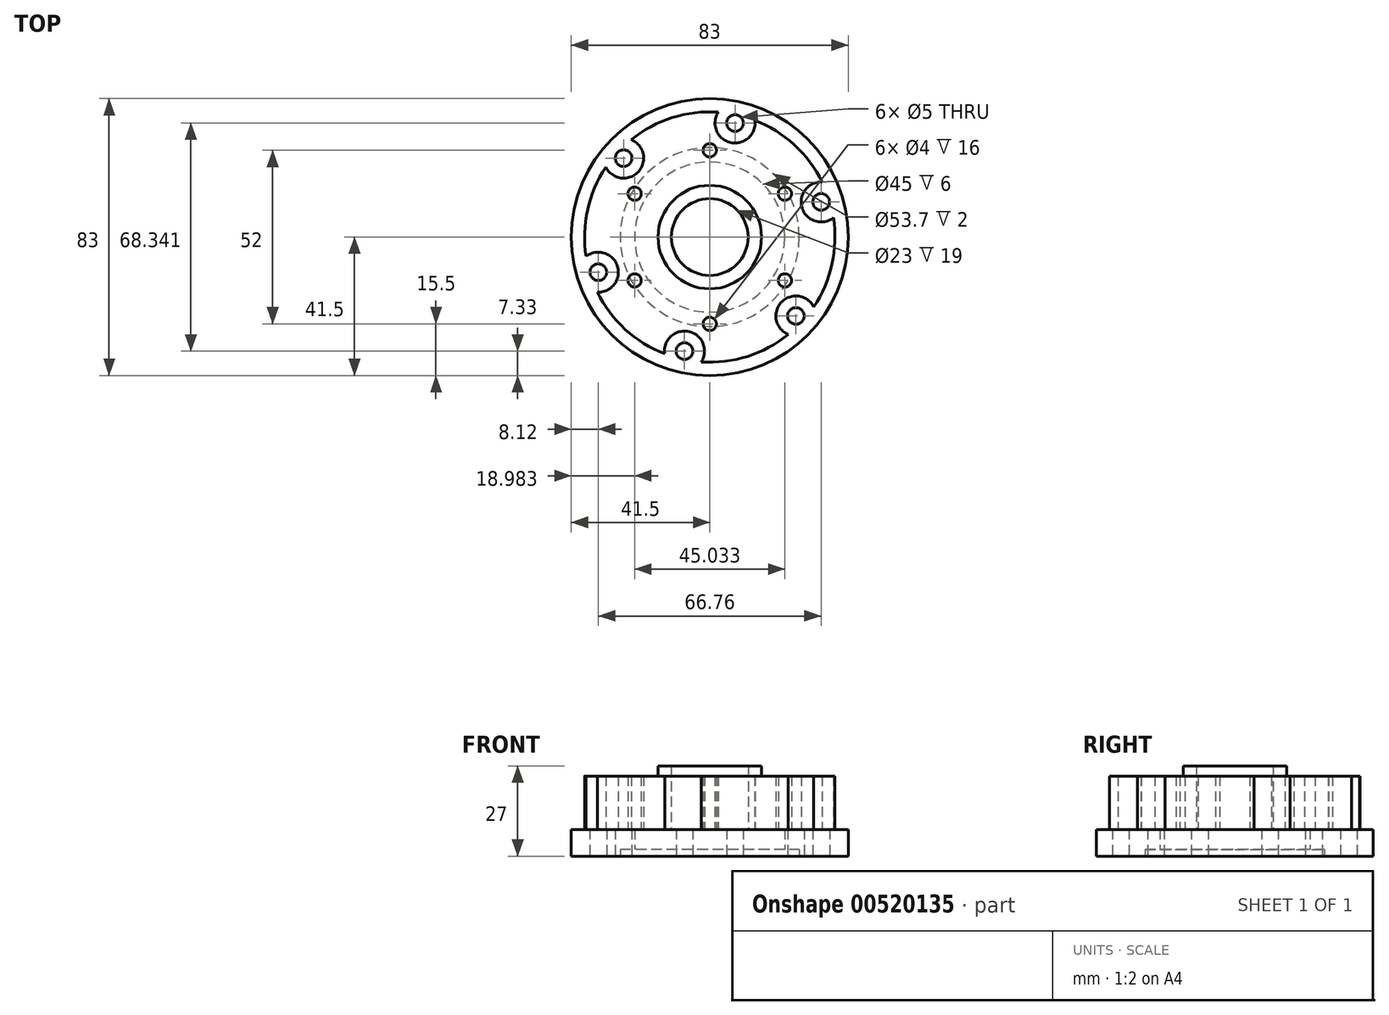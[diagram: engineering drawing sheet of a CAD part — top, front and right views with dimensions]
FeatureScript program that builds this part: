
annotation { "Feature Type Name" : "Feature", "Feature Type Description" : "" }
export const myFeature = defineFeature(function(context is Context, id is Id, definition is map)
    precondition{}
    {
        {
            var Q0;
            Q0=qCreatedBy(makeId("Top.planeOp"),FACE);
            var sketch = newSketch(context, id + "F0", { "sketchPlane" : qUnion([Q0])});
            skCircle(sketch, "E0", {"center": v(0, 0) * mm, "radius": 41.5 * mm});
            skLineSegment(sketch, "E1", {"start": v(0, 0) * mm, "end": v(-13.8, -62.28) * mm, "construction": true});
            skCircle(sketch, "E2", {"center": v(0, 0) * mm, "radius": 35 * mm, "construction": true});
            skCircle(sketch, "E3", {"center": v(-7.58, -34.17) * mm, "radius": 2.5 * mm});
            skCircle(sketch, "E4.1.0", {"center": v(25.8, -23.65) * mm, "radius": 2.5 * mm});
            skCircle(sketch, "E4.2.0", {"center": v(33.38, 10.52) * mm, "radius": 2.5 * mm});
            skCircle(sketch, "E5.1.3.0", {"center": v(7.58, 34.17) * mm, "radius": 2.5 * mm});
            skCircle(sketch, "E5.1.4.0", {"center": v(-25.8, 23.65) * mm, "radius": 2.5 * mm});
            skCircle(sketch, "E5.1.5.0", {"center": v(-33.38, -10.52) * mm, "radius": 2.5 * mm});
            skCircle(sketch, "E6", {"center": v(0, 0) * mm, "radius": 26.85 * mm});
            skCircle(sketch, "E7", {"center": v(0, 0) * mm, "radius": 22.5 * mm});
            skSolve(sketch);
        }
        {
            var Q0;
            Q0=makeQuery(id+"F0.imprint","IMPRINT",FACE,{"disambiguationData":[TD([[makeQuery(id+"F0.imprint","IMPRINT",EDGE,{"derivedFrom":sQuery(id+"F0.wireOp",EDGE,"E0")}),1.0]])]});
            var Q1;
            Q1=makeQuery(id+"F0.imprint","IMPRINT",FACE,{"disambiguationData":[TD([[makeQuery(id+"F0.imprint","IMPRINT",EDGE,{"derivedFrom":sQuery(id+"F0.wireOp",EDGE,"E6")}),1.0]])]});
            extrude(context, id + "F1", {"entities" : qUnion([Q0, Q1]), "depth" : 8 * mm, "offsetDistance" : 25 * mm});
        }
        {
            var Q0;
            Q0=makeQuery(id+"F0.imprint","IMPRINT",FACE,{"disambiguationData":[TD([[makeQuery(id+"F0.imprint","IMPRINT",EDGE,{"derivedFrom":sQuery(id+"F0.wireOp",EDGE,"E6")}),1.0]])]});
            extrude(context, id + "F2", {"entities" : qUnion([Q0]), "operationType" : NewBodyOperationType.REMOVE, "depth" : 2 * mm, "offsetDistance" : 25 * mm});
        }
        {
            var Q0;
            Q0=makeQuery(id+"F1.opExtrude","CAP_FACE",FACE,{"disambiguationData":[OSD([sQuery(id+"F0.wireOp",EDGE,"E0"),sQuery(id+"F0.wireOp",EDGE,"E3"),sQuery(id+"F0.wireOp",EDGE,"E4.1.0"),sQuery(id+"F0.wireOp",EDGE,"E4.2.0"),sQuery(id+"F0.wireOp",EDGE,"E5.1.3.0"),sQuery(id+"F0.wireOp",EDGE,"E5.1.4.0"),sQuery(id+"F0.wireOp",EDGE,"E5.1.5.0"),sQuery(id+"F0.wireOp",EDGE,"E7")])],"isStart":false});
            var sketch = newSketch(context, id + "F3", { "sketchPlane" : qUnion([Q0])});
            skCircle(sketch, "E8", {"center": v(0, 0) * mm, "radius": 37.5 * mm});
            skCircle(sketch, "E9", {"center": v(0, 0) * mm, "radius": 26 * mm, "construction": true});
            skCircle(sketch, "E10", {"center": v(0, 26) * mm, "radius": 2 * mm});
            skCircle(sketch, "E11.1.0", {"center": v(-22.52, 13) * mm, "radius": 2 * mm});
            skCircle(sketch, "E11.2.0", {"center": v(-22.52, -13) * mm, "radius": 2 * mm});
            skCircle(sketch, "E11.3.0", {"center": v(0, -26) * mm, "radius": 2 * mm});
            skCircle(sketch, "E11.4.0", {"center": v(22.52, -13) * mm, "radius": 2 * mm});
            skCircle(sketch, "E11.5.0", {"center": v(22.52, 13) * mm, "radius": 2 * mm});
            skCircle(sketch, "E12", {"center": v(0, 0) * mm, "radius": 11.5 * mm});
            skCircle(sketch, "E13", {"center": v(-25.8, 23.65) * mm, "radius": 6 * mm});
            skCircle(sketch, "E14.1.0", {"center": v(-33.38, -10.52) * mm, "radius": 6 * mm});
            skCircle(sketch, "E14.2.0", {"center": v(-7.58, -34.17) * mm, "radius": 6 * mm});
            skCircle(sketch, "E14.3.0", {"center": v(25.8, -23.65) * mm, "radius": 6 * mm});
            skCircle(sketch, "E14.4.0", {"center": v(33.38, 10.52) * mm, "radius": 6 * mm});
            skCircle(sketch, "E14.5.0", {"center": v(7.58, 34.17) * mm, "radius": 6 * mm});
            skSolve(sketch);
        }
        {
            var Q0;
            {var subQ6=sQuery(id+"F3.wireOp",EDGE,"E8");var subQ34=sQuery(id+"F3.wireOp",EDGE,"E14.4.0");var subQ35=makeQuery(id+"F3.imprint","INTERSECT",VERTEX,{"disambiguationData":[OD(1.0)],"derivedFrom":[subQ6,subQ34]});Q0=makeQuery(id+"F3.imprint","IMPRINT",FACE,{"disambiguationData":[TD([[makeQuery(id+"F3.imprint","IMPRINT",EDGE,{"disambiguationData":[TD([[subQ35,-1.0]])],"derivedFrom":subQ6}),1.0]])]});}
            var Q1;
            Q1=makeQuery(id+"F3.imprint","IMPRINT",FACE,{"disambiguationData":[TD([[makeQuery(id+"F3.imprint","IMPRINT",EDGE,{"derivedFrom":sQuery(id+"F3.wireOp",EDGE,"E12")}),-1.0]])]});
            extrude(context, id + "F4", {"entities" : qUnion([Q0, Q1]), "operationType" : NewBodyOperationType.ADD, "depth" : 16 * mm, "offsetDistance" : 25 * mm});
        }
        {
            var Q0;
            Q0=makeQuery(id+"F4.opExtrude","CAP_FACE",FACE,{"disambiguationData":[OSD([sQuery(id+"F3.wireOp",EDGE,"E8"),sQuery(id+"F3.wireOp",EDGE,"E10"),sQuery(id+"F3.wireOp",EDGE,"E11.1.0"),sQuery(id+"F3.wireOp",EDGE,"E11.2.0"),sQuery(id+"F3.wireOp",EDGE,"E11.3.0"),sQuery(id+"F3.wireOp",EDGE,"E11.4.0"),sQuery(id+"F3.wireOp",EDGE,"E11.5.0"),sQuery(id+"F3.wireOp",EDGE,"E12"),sQuery(id+"F3.wireOp",EDGE,"E13"),sQuery(id+"F3.wireOp",EDGE,"E14.1.0"),sQuery(id+"F3.wireOp",EDGE,"E14.2.0"),sQuery(id+"F3.wireOp",EDGE,"E14.3.0"),sQuery(id+"F3.wireOp",EDGE,"E14.4.0"),sQuery(id+"F3.wireOp",EDGE,"E14.5.0")])],"isStart":false});
            var sketch = newSketch(context, id + "F5", { "sketchPlane" : qUnion([Q0])});
            skCircle(sketch, "E15", {"center": v(0, 0) * mm, "radius": 15.5 * mm});
            skSolve(sketch);
        }
        {
            var Q0;
            Q0=makeQuery(id+"F5.imprint","IMPRINT",FACE,{"disambiguationData":[TD([[makeQuery(id+"F5.imprint","IMPRINT",EDGE,{"derivedFrom":sQuery(id+"F5.wireOp",EDGE,"E15")}),1.0]])]});
            extrude(context, id + "F6", {"entities" : qUnion([Q0]), "operationType" : NewBodyOperationType.ADD, "depth" : 3 * mm, "offsetDistance" : 25 * mm});
        }
    });
